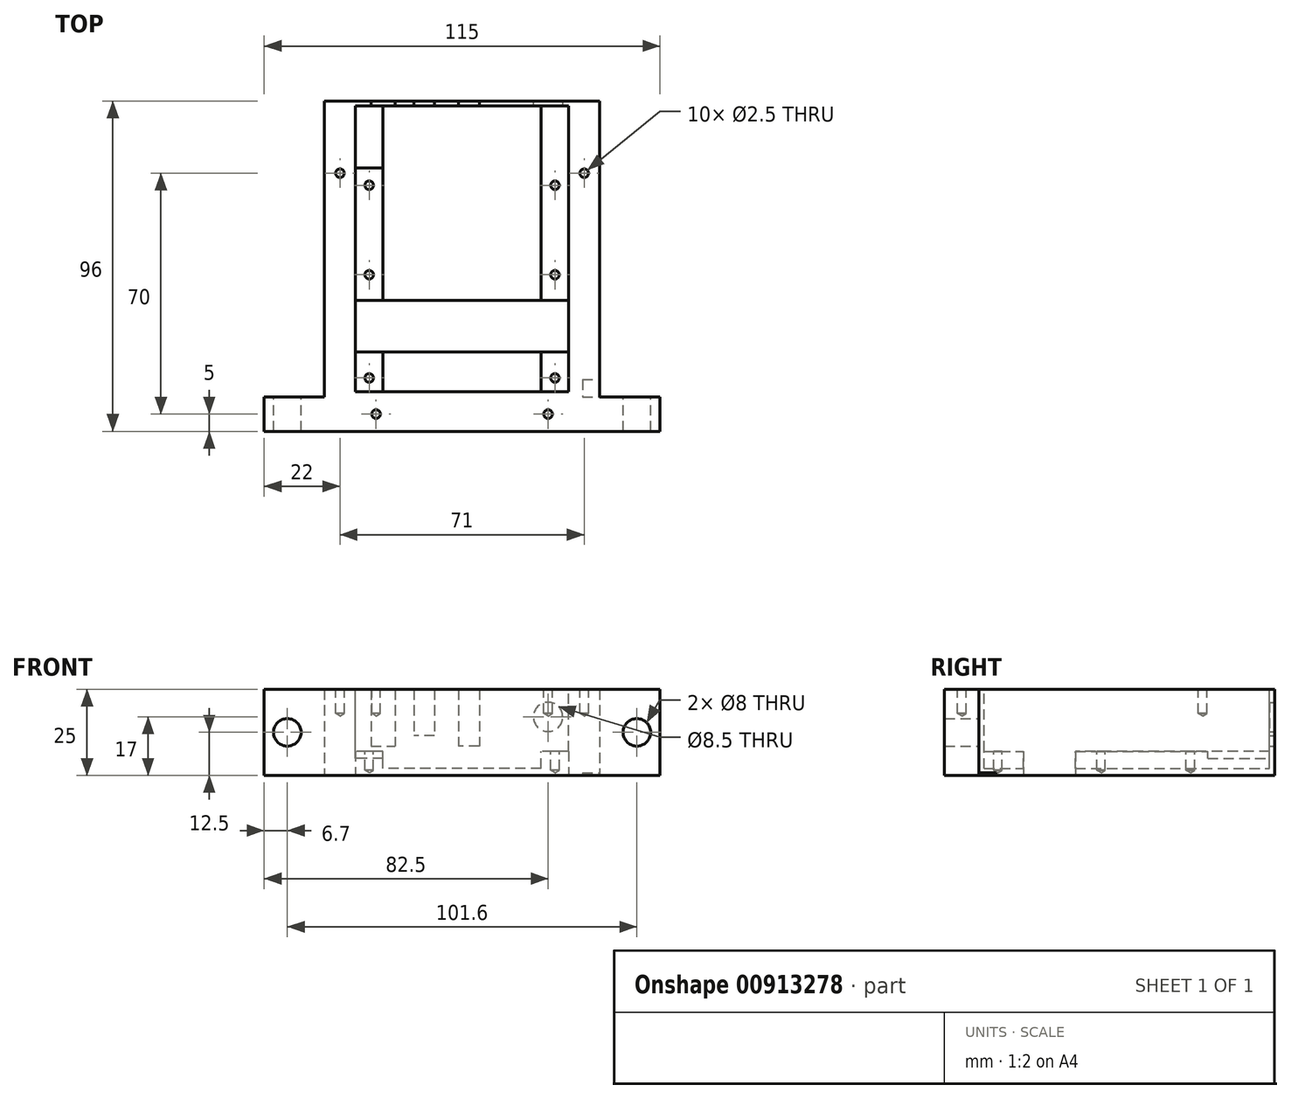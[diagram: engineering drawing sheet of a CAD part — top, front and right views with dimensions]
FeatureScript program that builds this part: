
annotation { "Feature Type Name" : "Feature", "Feature Type Description" : "" }
export const myFeature = defineFeature(function(context is Context, id is Id, definition is map)
    precondition{}
    {
        {
            var Q0;
            Q0=qCreatedBy(makeId("Top.planeOp"),FACE);
            var sketch = newSketch(context, id + "F0", { "sketchPlane" : qUnion([Q0])});
            skLineSegment(sketch, "E0.bottom", {"start": v(-40, 48) * mm, "end": v(40, 48) * mm});
            skLineSegment(sketch, "E0.left", {"start": v(-40, 48) * mm, "end": v(-40, -38) * mm});
            skLineSegment(sketch, "E0.right", {"start": v(40, 48) * mm, "end": v(40, -38) * mm});
            skLineSegment(sketch, "E1.bottom", {"start": v(-57.5, -38) * mm, "end": v(-40, -38) * mm});
            skLineSegment(sketch, "E1.top", {"start": v(-57.5, -48) * mm, "end": v(57.5, -48) * mm});
            skLineSegment(sketch, "E1.left", {"start": v(-57.5, -38) * mm, "end": v(-57.5, -48) * mm});
            skLineSegment(sketch, "E1.right", {"start": v(57.5, -38) * mm, "end": v(57.5, -48) * mm});
            skLineSegment(sketch, "E2", {"start": v(0, 66.03) * mm, "end": v(0, -67.52) * mm, "construction": true});
            skLineSegment(sketch, "E3.trimOffspring", {"start": v(40, -38) * mm, "end": v(57.5, -38) * mm});
            skLineSegment(sketch, "E4", {"start": v(-41.52, 0) * mm, "end": v(40.59, 0) * mm, "construction": true});
            skSolve(sketch);
        }
        {
            var Q0;
            Q0=qSketchRegion(id+"F0",true);
            extrude(context, id + "F1", {"entities" : qUnion([Q0]), "depth" : 25 * mm, "offsetDistance" : 25 * mm});
        }
        {
            var Q0;
            Q0=makeQuery(id+"F1.opExtrude","CAP_FACE",FACE,{"disambiguationData":[OSD([sQuery(id+"F0.wireOp",EDGE,"E0.bottom"),sQuery(id+"F0.wireOp",EDGE,"E0.left"),sQuery(id+"F0.wireOp",EDGE,"E0.right"),sQuery(id+"F0.wireOp",EDGE,"E1.bottom"),sQuery(id+"F0.wireOp",EDGE,"E1.top"),sQuery(id+"F0.wireOp",EDGE,"E1.left"),sQuery(id+"F0.wireOp",EDGE,"E1.right"),sQuery(id+"F0.wireOp",EDGE,"E3.trimOffspring")])],"isStart":false});
            var sketch = newSketch(context, id + "F2", { "sketchPlane" : qUnion([Q0])});
            skLineSegment(sketch, "E5", {"start": v(0, 48) * mm, "end": v(0, -48) * mm, "construction": true});
            skLineSegment(sketch, "E6", {"start": v(-40, 5) * mm, "end": v(40, 5) * mm, "construction": true});
            skLineSegment(sketch, "E7.bottom", {"start": v(31, 46.5) * mm, "end": v(-31, 46.5) * mm});
            skLineSegment(sketch, "E7.top", {"start": v(31, -36.5) * mm, "end": v(-31, -36.5) * mm});
            skLineSegment(sketch, "E7.left", {"start": v(31, 46.5) * mm, "end": v(31, -36.5) * mm});
            skLineSegment(sketch, "E7.right", {"start": v(-31, 46.5) * mm, "end": v(-31, -36.5) * mm});
            skPoint(sketch, "E7.middle", {"position": v(0, 5) * mm});
            skSolve(sketch);
        }
        {
            var Q0;
            Q0=makeQuery(id+"F2.imprint","IMPRINT",FACE,{"disambiguationData":[TD([[makeQuery(id+"F2.imprint","IMPRINT",EDGE,{"derivedFrom":sQuery(id+"F2.wireOp",EDGE,"E7.bottom")}),1.0]])]});
            extrude(context, id + "F3", {"entities" : qUnion([Q0]), "operationType" : NewBodyOperationType.REMOVE, "oppositeDirection" : true, "depth" : 18 * mm, "offsetDistance" : 25 * mm});
        }
        {
            var Q0;
            Q0=makeQuery(id+"F3.boolean.opBoolean","COPY",FACE,{"derivedFrom":makeQuery(id+"F3.opExtrude","CAP_FACE",FACE,{"disambiguationData":[OSD([sQuery(id+"F2.wireOp",EDGE,"E7.bottom"),sQuery(id+"F2.wireOp",EDGE,"E7.top"),sQuery(id+"F2.wireOp",EDGE,"E7.left"),sQuery(id+"F2.wireOp",EDGE,"E7.right")])],"isStart":false})});
            var sketch = newSketch(context, id + "F4", { "sketchPlane" : qUnion([Q0])});
            skLineSegment(sketch, "E8", {"start": v(0, 46.5) * mm, "end": v(0, -36.5) * mm, "construction": true});
            skLineSegment(sketch, "E9.bottom", {"start": v(23, -36.5) * mm, "end": v(-23, -36.5) * mm});
            skLineSegment(sketch, "E9.top", {"start": v(23, 46.5) * mm, "end": v(-23, 46.5) * mm});
            skLineSegment(sketch, "E9.left", {"start": v(23, -36.5) * mm, "end": v(23, 46.5) * mm});
            skLineSegment(sketch, "E9.right", {"start": v(-23, -36.5) * mm, "end": v(-23, 46.5) * mm});
            skSolve(sketch);
        }
        {
            var Q0;
            Q0=makeQuery(id+"F4.imprint","IMPRINT",FACE,{"disambiguationData":[TD([[makeQuery(id+"F4.imprint","IMPRINT",EDGE,{"derivedFrom":sQuery(id+"F4.wireOp",EDGE,"E9.bottom")}),-1.0]])]});
            extrude(context, id + "F5", {"entities" : qUnion([Q0]), "operationType" : NewBodyOperationType.REMOVE, "oppositeDirection" : true, "depth" : 5 * mm, "offsetDistance" : 25 * mm});
        }
        {
            var Q0;
            Q0=makeQuery(id+"F3.boolean.opBoolean","COPY",FACE,{"derivedFrom":makeQuery(id+"F3.opExtrude","CAP_FACE",FACE,{"disambiguationData":[OSD([sQuery(id+"F2.wireOp",EDGE,"E7.bottom"),sQuery(id+"F2.wireOp",EDGE,"E7.top"),sQuery(id+"F2.wireOp",EDGE,"E7.left"),sQuery(id+"F2.wireOp",EDGE,"E7.right")])],"isStart":false})});
            var sketch = newSketch(context, id + "F6", { "sketchPlane" : qUnion([Q0])});
            skLineSegment(sketch, "E10", {"start": v(-27, -36.5) * mm, "end": v(-27, 28.23) * mm, "construction": true});
            skLineSegment(sketch, "E11", {"start": v(27, -36.5) * mm, "end": v(27, 26.7) * mm, "construction": true});
            skLineSegment(sketch, "E12", {"start": v(0, 28) * mm, "end": v(0, -50.3) * mm, "construction": true});
            skLineSegment(sketch, "E13", {"start": v(-29.07, 23.5) * mm, "end": v(28.49, 23.5) * mm, "construction": true});
            skLineSegment(sketch, "E14.0", {"start": v(-29.07, -2.5) * mm, "end": v(28.49, -2.5) * mm});
            skLineSegment(sketch, "E15.0", {"start": v(-29.07, -32.5) * mm, "end": v(28.49, -32.5) * mm});
            skPoint(sketch, "E16", {"position": v(-27, -32.5) * mm});
            skPoint(sketch, "E17", {"position": v(-27, 23.5) * mm});
            skPoint(sketch, "E18", {"position": v(27, 23.5) * mm});
            skPoint(sketch, "E19", {"position": v(27, -2.5) * mm});
            skPoint(sketch, "E20", {"position": v(27, -32.5) * mm});
            skPoint(sketch, "E21", {"position": v(-27, -2.5) * mm});
            skSolve(sketch);
        }
        {
            var Q0;
            Q0=sQuery(id+"F6.wireOp",VERTEX,"E16");
            var Q1;
            Q1=sQuery(id+"F6.wireOp",VERTEX,"E21");
            var Q2;
            Q2=sQuery(id+"F6.wireOp",VERTEX,"E17");
            var Q3;
            Q3=sQuery(id+"F6.wireOp",VERTEX,"E20");
            var Q4;
            Q4=sQuery(id+"F6.wireOp",VERTEX,"E19");
            var Q5;
            Q5=sQuery(id+"F6.wireOp",VERTEX,"E18");
            var Q6;
            Q6=makeQuery(id+"F1.opExtrude","SWEPT_BODY",BODY,{"disambiguationData":[OSD([sQuery(id+"F0.wireOp",EDGE,"E0.bottom"),sQuery(id+"F0.wireOp",EDGE,"E0.left"),sQuery(id+"F0.wireOp",EDGE,"E0.right"),sQuery(id+"F0.wireOp",EDGE,"E1.bottom"),sQuery(id+"F0.wireOp",EDGE,"E1.top"),sQuery(id+"F0.wireOp",EDGE,"E1.left"),sQuery(id+"F0.wireOp",EDGE,"E1.right"),sQuery(id+"F0.wireOp",EDGE,"E3.trimOffspring")])]});
            hole(context, id + "F7", {"style" : HoleStyle.SIMPLE, "endStyle" : HoleEndStyle.BLIND, "holeDiameter" : 2.5 * mm, "majorDiameter" : 5 * mm, "holeDepth" : 5.5 * mm, "isTappedThrough" : true, "tappedDepth" : 12 * mm, "tapClearance" : 3, "startFromSketch" : true, "locations" : qUnion([Q0, Q1, Q2, Q3, Q4, Q5]), "scope" : qUnion([Q6])});
        }
        {
            var Q0;
            Q0=makeQuery(id+"F1.opExtrude","CAP_FACE",FACE,{"disambiguationData":[OSD([sQuery(id+"F0.wireOp",EDGE,"E0.bottom"),sQuery(id+"F0.wireOp",EDGE,"E0.left"),sQuery(id+"F0.wireOp",EDGE,"E0.right"),sQuery(id+"F0.wireOp",EDGE,"E1.bottom"),sQuery(id+"F0.wireOp",EDGE,"E1.top"),sQuery(id+"F0.wireOp",EDGE,"E1.left"),sQuery(id+"F0.wireOp",EDGE,"E1.right"),sQuery(id+"F0.wireOp",EDGE,"E3.trimOffspring")])],"isStart":true});
            var sketch = newSketch(context, id + "F8", { "sketchPlane" : qUnion([Q0])});
            skLineSegment(sketch, "E22.bottom", {"start": v(-31, 25) * mm, "end": v(31, 25) * mm});
            skLineSegment(sketch, "E22.top", {"start": v(-31, 10) * mm, "end": v(31, 10) * mm});
            skLineSegment(sketch, "E22.left", {"start": v(-31, 25) * mm, "end": v(-31, 10) * mm});
            skLineSegment(sketch, "E22.right", {"start": v(31, 25) * mm, "end": v(31, 10) * mm});
            skPoint(sketch, "E23.endSnap0", {"position": v(0, 10) * mm});
            skLineSegment(sketch, "E24", {"start": v(0, 48) * mm, "end": v(0, 0) * mm, "construction": true});
            skSolve(sketch);
        }
        {
            var Q0;
            Q0=makeQuery(id+"F8.imprint","IMPRINT",FACE,{"disambiguationData":[TD([[makeQuery(id+"F8.imprint","IMPRINT",EDGE,{"derivedFrom":sQuery(id+"F8.wireOp",EDGE,"E22.bottom")}),-1.0]])]});
            extrude(context, id + "F9", {"entities" : qUnion([Q0]), "operationType" : NewBodyOperationType.REMOVE, "endBound" : BoundingType.THROUGH_ALL, "oppositeDirection" : true, "depth" : 25 * mm, "offsetDistance" : 25 * mm});
        }
        {
            var Q0;
            Q0=makeQuery(id+"F1.opExtrude","SWEPT_FACE",FACE,{"disambiguationData":[OSD([sQuery(id+"F0.wireOp",EDGE,"E3.trimOffspring")])]});
            var sketch = newSketch(context, id + "F10", { "sketchPlane" : qUnion([Q0])});
            skLineSegment(sketch, "E25", {"start": v(-51.24, 12.5) * mm, "end": v(51.38, 12.5) * mm, "construction": true});
            skLineSegment(sketch, "E26", {"start": v(50.8, 1.14) * mm, "end": v(50.8, 21.87) * mm, "construction": true});
            skLineSegment(sketch, "E27", {"start": v(-50.8, 2.75) * mm, "end": v(-50.8, 19.82) * mm, "construction": true});
            skLineSegment(sketch, "E28", {"start": v(0, 27.92) * mm, "end": v(0, 18.42) * mm, "construction": true});
            skPoint(sketch, "E29", {"position": v(50.8, 12.5) * mm});
            skPoint(sketch, "E30", {"position": v(-50.8, 12.5) * mm});
            skSolve(sketch);
        }
        {
            var Q0;
            Q0=sQuery(id+"F10.wireOp",VERTEX,"E29");
            var Q1;
            Q1=sQuery(id+"F10.wireOp",VERTEX,"E30");
            var Q2;
            Q2=makeQuery(id+"F1.opExtrude","SWEPT_BODY",BODY,{"disambiguationData":[OSD([sQuery(id+"F0.wireOp",EDGE,"E0.bottom"),sQuery(id+"F0.wireOp",EDGE,"E0.left"),sQuery(id+"F0.wireOp",EDGE,"E0.right"),sQuery(id+"F0.wireOp",EDGE,"E1.bottom"),sQuery(id+"F0.wireOp",EDGE,"E1.top"),sQuery(id+"F0.wireOp",EDGE,"E1.left"),sQuery(id+"F0.wireOp",EDGE,"E1.right"),sQuery(id+"F0.wireOp",EDGE,"E3.trimOffspring")])]});
            hole(context, id + "F11", {"style" : HoleStyle.SIMPLE, "endStyle" : HoleEndStyle.THROUGH, "holeDiameter" : 8 * mm, "majorDiameter" : 5 * mm, "isTappedThrough" : true, "tappedDepth" : 12 * mm, "tapClearance" : 3, "startFromSketch" : true, "locations" : qUnion([Q0, Q1]), "scope" : qUnion([Q2])});
        }
        {
            var Q0;
            Q0=makeQuery(id+"F1.opExtrude","SWEPT_FACE",FACE,{"disambiguationData":[OSD([sQuery(id+"F0.wireOp",EDGE,"E0.bottom")])]});
            var sketch = newSketch(context, id + "F12", { "sketchPlane" : qUnion([Q0])});
            skLineSegment(sketch, "E31.bottom", {"start": v(26.5, 25) * mm, "end": v(19.5, 25) * mm});
            skLineSegment(sketch, "E31.top", {"start": v(26.5, 8.5) * mm, "end": v(19.5, 8.5) * mm});
            skLineSegment(sketch, "E31.left", {"start": v(26.5, 25) * mm, "end": v(26.5, 8.5) * mm});
            skLineSegment(sketch, "E31.right", {"start": v(19.5, 25) * mm, "end": v(19.5, 8.5) * mm});
            skLineSegment(sketch, "E32.bottom", {"start": v(8, 25) * mm, "end": v(14, 25) * mm});
            skLineSegment(sketch, "E32.left", {"start": v(8, 25) * mm, "end": v(8, 11.5) * mm});
            skLineSegment(sketch, "E32.right", {"start": v(14, 25) * mm, "end": v(14, 11.5) * mm});
            skLineSegment(sketch, "E33.bottom", {"start": v(-5, 25) * mm, "end": v(1, 25) * mm});
            skLineSegment(sketch, "E33.top", {"start": v(-5, 8.5) * mm, "end": v(1, 8.5) * mm});
            skLineSegment(sketch, "E33.left", {"start": v(-5, 25) * mm, "end": v(-5, 8.5) * mm});
            skLineSegment(sketch, "E33.right", {"start": v(1, 25) * mm, "end": v(1, 8.5) * mm});
            skLineSegment(sketch, "E34", {"start": v(8, 11.5) * mm, "end": v(14, 11.5) * mm});
            skSolve(sketch);
        }
        {
            var Q0;
            Q0=makeQuery(id+"F12.imprint","IMPRINT",FACE,{"disambiguationData":[TD([[makeQuery(id+"F12.imprint","IMPRINT",EDGE,{"derivedFrom":sQuery(id+"F12.wireOp",EDGE,"E33.bottom")}),1.0]])]});
            var Q1;
            Q1=makeQuery(id+"F12.imprint","IMPRINT",FACE,{"disambiguationData":[TD([[makeQuery(id+"F12.imprint","IMPRINT",EDGE,{"derivedFrom":sQuery(id+"F12.wireOp",EDGE,"E32.bottom")}),1.0]])]});
            var Q2;
            Q2=makeQuery(id+"F12.imprint","IMPRINT",FACE,{"disambiguationData":[TD([[makeQuery(id+"F12.imprint","IMPRINT",EDGE,{"derivedFrom":sQuery(id+"F12.wireOp",EDGE,"E31.bottom")}),1.0]])]});
            var Q3;
            Q3=makeQuery(id+"F3.boolean.opBoolean","COPY",FACE,{"derivedFrom":makeQuery(id+"F3.opExtrude","SWEPT_FACE",FACE,{"disambiguationData":[OSD([sQuery(id+"F2.wireOp",EDGE,"E7.bottom")])]})});
            extrude(context, id + "F13", {"entities" : qUnion([Q0, Q1, Q2]), "operationType" : NewBodyOperationType.REMOVE, "endBound" : BoundingType.UP_TO_SURFACE, "oppositeDirection" : true, "depth" : 25 * mm, "endBoundEntityFace" : qUnion([Q3]), "offsetDistance" : 25 * mm});
        }
        {
            var Q0;
            {var subQ1=sQuery(id+"F2.wireOp",EDGE,"E7.right");var subQ2=makeQuery(id+"F3.boolean.opBoolean","COPY",FACE,{"derivedFrom":makeQuery(id+"F3.opExtrude","SWEPT_FACE",FACE,{"disambiguationData":[OSD([subQ1])]})});var subQ3=sQuery(id+"F2.wireOp",EDGE,"E7.bottom");var subQ4=makeQuery(id+"F3.boolean.opBoolean","COPY",FACE,{"derivedFrom":makeQuery(id+"F3.opExtrude","SWEPT_FACE",FACE,{"disambiguationData":[OSD([subQ3])]})});var subQ5=sQuery(id+"F2.wireOp",EDGE,"E7.top");Q0=makeQuery(id+"F9.boolean.opBoolean","SPLIT",FACE,{"disambiguationData":[TD([subQ4])],"derivedFrom":makeQuery(id+"F5.boolean.opBoolean","SPLIT",FACE,{"disambiguationData":[TD([subQ2])],"derivedFrom":makeQuery(id+"F3.boolean.opBoolean","COPY",FACE,{"derivedFrom":makeQuery(id+"F3.opExtrude","CAP_FACE",FACE,{"disambiguationData":[OSD([subQ3,subQ5,sQuery(id+"F2.wireOp",EDGE,"E7.left"),subQ1])],"isStart":false})})})});}
            var sketch = newSketch(context, id + "F14", { "sketchPlane" : qUnion([Q0])});
            skLineSegment(sketch, "E35.bottom", {"start": v(-31, 46.5) * mm, "end": v(-23, 46.5) * mm});
            skLineSegment(sketch, "E35.top", {"start": v(-31, 28.5) * mm, "end": v(-23, 28.5) * mm});
            skLineSegment(sketch, "E35.left", {"start": v(-31, 46.5) * mm, "end": v(-31, 28.5) * mm});
            skLineSegment(sketch, "E35.right", {"start": v(-23, 46.5) * mm, "end": v(-23, 28.5) * mm});
            skSolve(sketch);
        }
        {
            var Q0;
            Q0=makeQuery(id+"F14.imprint","IMPRINT",FACE,{"disambiguationData":[TD([[makeQuery(id+"F14.imprint","IMPRINT",EDGE,{"derivedFrom":sQuery(id+"F14.wireOp",EDGE,"E35.bottom")}),1.0]])]});
            extrude(context, id + "F15", {"entities" : qUnion([Q0]), "operationType" : NewBodyOperationType.REMOVE, "oppositeDirection" : true, "depth" : 2 * mm, "offsetDistance" : 25 * mm});
        }
        {
            var Q0;
            Q0=makeQuery(id+"F1.opExtrude","SWEPT_FACE",FACE,{"disambiguationData":[OSD([sQuery(id+"F0.wireOp",EDGE,"E0.bottom")])]});
            var sketch = newSketch(context, id + "F16", { "sketchPlane" : qUnion([Q0])});
            skCircle(sketch, "E36", {"center": v(-25, 17) * mm, "radius": 4.25 * mm});
            skSolve(sketch);
        }
        {
            var Q0;
            Q0=makeQuery(id+"F16.imprint","IMPRINT",FACE,{"disambiguationData":[TD([[makeQuery(id+"F16.imprint","IMPRINT",EDGE,{"derivedFrom":sQuery(id+"F16.wireOp",EDGE,"E36")}),1.0]])]});
            var Q1;
            Q1=makeQuery(id+"F15.boolean.opBoolean","MERGE",FACE,{"derivedFrom":[makeQuery(id+"F5.boolean.opBoolean","MERGE",FACE,{"derivedFrom":[makeQuery(id+"F3.boolean.opBoolean","COPY",FACE,{"derivedFrom":makeQuery(id+"F3.opExtrude","SWEPT_FACE",FACE,{"disambiguationData":[OSD([sQuery(id+"F2.wireOp",EDGE,"E7.bottom")])]})})],"fromTools":[makeQuery(id+"F5.opExtrude","SWEPT_FACE",FACE,{"disambiguationData":[OSD([sQuery(id+"F4.wireOp",EDGE,"E9.top")])]})]})],"fromTools":[makeQuery(id+"F15.opExtrude","SWEPT_FACE",FACE,{"disambiguationData":[OSD([sQuery(id+"F14.wireOp",EDGE,"E35.bottom")])]})]});
            extrude(context, id + "F17", {"entities" : qUnion([Q0]), "operationType" : NewBodyOperationType.REMOVE, "endBound" : BoundingType.UP_TO_SURFACE, "oppositeDirection" : true, "depth" : 25 * mm, "endBoundEntityFace" : qUnion([Q1]), "offsetDistance" : 25 * mm});
        }
        {
            var Q0;
            {var subQ0=sQuery(id+"FSGkL8cZMvJVaoK_1.wireOp",EDGE,"19ZCul45-CmC5-CmSV-8faD-4O6wiWYA0Wkr.top");var subQ3=sQuery(id+"F0.wireOp",EDGE,"E0.right");Q0=makeQuery(id+"FY24BLFiGkHRrBw_1.boolean.opBoolean","SPLIT",FACE,{"disambiguationData":[TD([makeQuery(id+"FY24BLFiGkHRrBw_1.opExtrude","SWEPT_FACE",FACE,{"disambiguationData":[OSD([subQ0])]})])],"derivedFrom":makeQuery(id+"F1.opExtrude","SWEPT_FACE",FACE,{"disambiguationData":[OSD([subQ3])]})});}
            var sketch = newSketch(context, id + "F18", { "sketchPlane" : qUnion([Q0])});
            skLineSegment(sketch, "E37.bottom", {"start": v(-38, 0) * mm, "end": v(-33, 0) * mm});
            skLineSegment(sketch, "E37.top", {"start": v(-38, 0.7) * mm, "end": v(-33, 0.7) * mm});
            skLineSegment(sketch, "E37.left", {"start": v(-38, 0) * mm, "end": v(-38, 0.7) * mm});
            skLineSegment(sketch, "E37.right", {"start": v(-33, 0) * mm, "end": v(-33, 0.7) * mm});
            skSolve(sketch);
        }
        {
            var Q0;
            Q0=makeQuery(id+"F18.imprint","IMPRINT",FACE,{"disambiguationData":[TD([[makeQuery(id+"F18.imprint","IMPRINT",EDGE,{"derivedFrom":sQuery(id+"F18.wireOp",EDGE,"E37.bottom")}),-1.0]])]});
            extrude(context, id + "F19", {"entities" : qUnion([Q0]), "operationType" : NewBodyOperationType.REMOVE, "oppositeDirection" : true, "depth" : 5 * mm, "offsetDistance" : 25 * mm});
        }
        {
            var Q0;
            {var subQ0=sQuery(id+"F0.wireOp",EDGE,"E3.trimOffspring");var subQ1=sQuery(id+"F0.wireOp",EDGE,"E1.right");var subQ2=sQuery(id+"F0.wireOp",EDGE,"E1.left");var subQ3=sQuery(id+"F0.wireOp",EDGE,"E1.top");var subQ4=sQuery(id+"F0.wireOp",EDGE,"E0.bottom");var subQ5=sQuery(id+"F0.wireOp",EDGE,"E1.bottom");var subQ6=sQuery(id+"F0.wireOp",EDGE,"E0.left");var subQ7=sQuery(id+"F0.wireOp",EDGE,"E0.right");Q0=makeQuery(id+"F13.boolean.opBoolean","SPLIT",FACE,{"disambiguationData":[TD([makeQuery(id+"F1.opExtrude","SWEPT_FACE",FACE,{"disambiguationData":[OSD([subQ6])]})])],"derivedFrom":makeQuery(id+"F1.opExtrude","CAP_FACE",FACE,{"disambiguationData":[OSD([subQ4,subQ6,subQ7,subQ5,subQ3,subQ2,subQ1,subQ0])],"isStart":false})});}
            var sketch = newSketch(context, id + "F20", { "sketchPlane" : qUnion([Q0])});
            skLineSegment(sketch, "E38", {"start": v(0, -48) * mm, "end": v(0, 101.86) * mm, "construction": true});
            skLineSegment(sketch, "E39", {"start": v(57.5, -43) * mm, "end": v(-57.5, -43) * mm, "construction": true});
            skLineSegment(sketch, "E40", {"start": v(31, 46.5) * mm, "end": v(40, 46.5) * mm, "construction": true});
            skLineSegment(sketch, "E41", {"start": v(31, -36.5) * mm, "end": v(40, -36.5) * mm, "construction": true});
            skLineSegment(sketch, "E42", {"start": v(35.5, 46.5) * mm, "end": v(35.5, -36.5) * mm, "construction": true});
            skLineSegment(sketch, "E43", {"start": v(-31, -36.5) * mm, "end": v(-40, -36.5) * mm, "construction": true});
            skLineSegment(sketch, "E44", {"start": v(-31, 46.5) * mm, "end": v(-40, 46.5) * mm, "construction": true});
            skLineSegment(sketch, "E45", {"start": v(-35.5, 46.5) * mm, "end": v(-35.5, -36.5) * mm, "construction": true});
            skPoint(sketch, "E46", {"position": v(25, -43) * mm});
            skPoint(sketch, "E47", {"position": v(-25, -43) * mm});
            skPoint(sketch, "E48", {"position": v(35.5, 27) * mm});
            skPoint(sketch, "E49", {"position": v(-35.5, 27) * mm});
            skSolve(sketch);
        }
        {
            var Q0;
            Q0=sQuery(id+"F20.wireOp",VERTEX,"E46");
            var Q1;
            Q1=sQuery(id+"F20.wireOp",VERTEX,"E47");
            var Q2;
            Q2=sQuery(id+"F20.wireOp",VERTEX,"E48");
            var Q3;
            Q3=sQuery(id+"F20.wireOp",VERTEX,"E49");
            var Q4;
            Q4=makeQuery(id+"F1.opExtrude","SWEPT_BODY",BODY,{"disambiguationData":[OSD([sQuery(id+"F0.wireOp",EDGE,"E0.bottom"),sQuery(id+"F0.wireOp",EDGE,"E0.left"),sQuery(id+"F0.wireOp",EDGE,"E0.right"),sQuery(id+"F0.wireOp",EDGE,"E1.bottom"),sQuery(id+"F0.wireOp",EDGE,"E1.top"),sQuery(id+"F0.wireOp",EDGE,"E1.left"),sQuery(id+"F0.wireOp",EDGE,"E1.right"),sQuery(id+"F0.wireOp",EDGE,"E3.trimOffspring")])]});
            hole(context, id + "F21", {"style" : HoleStyle.SIMPLE, "endStyle" : HoleEndStyle.BLIND, "holeDiameter" : 2.5 * mm, "majorDiameter" : 5 * mm, "holeDepth" : 7 * mm, "isTappedThrough" : true, "tappedDepth" : 12 * mm, "tapClearance" : 3, "startFromSketch" : true, "locations" : qUnion([Q0, Q1, Q2, Q3]), "scope" : qUnion([Q4])});
        }
    });
